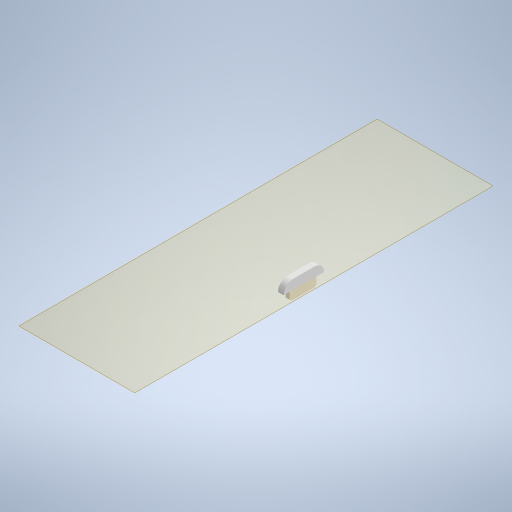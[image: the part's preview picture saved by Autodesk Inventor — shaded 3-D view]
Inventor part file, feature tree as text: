
AUTODESK INVENTOR PART (.ipt)
format: ipt  version: 2024 (Build 280153000, 153)  size: 278,016 bytes
history: native  units: mm
features: other x3, plane x2, extrude x2, sketch x2, reference x2, fillet x1, chamfer x1
ambient origin geometry x8: Origin, YZ Plane, XZ Plane, XY Plane, X Axis, Y Axis, Z Axis, Center Point
bodies: Solid1 (feature_tree)
feature tree (13):
  plane  "Work Plane1"
  extrude  "Extrusion1"  Depth=3.0mm
  sketch  "Sketch2"  dims[d2=5.0mm d3=0.0mm d4=0.5mm d5=5.0mm d6=0.0mm d7=5.0mm d8=1.0mm d9=2.0mm d10=45.0deg]
  plane  "Work Plane2"
  extrude  "Extrusion2"  Depth=0.5mm
  fillet  "Fillet1"  Radius=5.0mm
  chamfer  "Chamfer1"  Distance=5.0mm
  sketch  "Sketch1"  dims[d0=3.0mm d1=3.0mm]
  reference  "Reference1"
  reference  "Reference2"
  other  "<userpath> windows\Documents\Inventor\Robotska_roka\Assembly4.iam"
  other  "Assembly4.iam"
  other  "pokrow:1"
